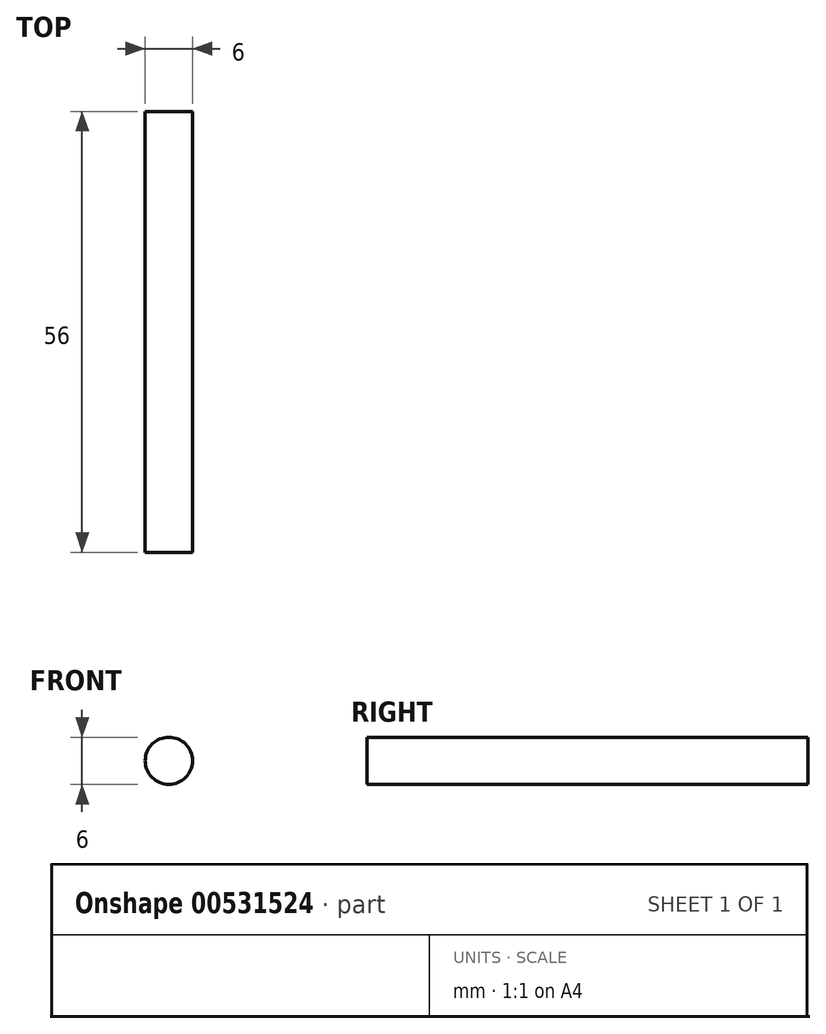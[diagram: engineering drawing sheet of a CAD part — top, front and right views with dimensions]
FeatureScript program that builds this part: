
annotation { "Feature Type Name" : "Feature", "Feature Type Description" : "" }
export const myFeature = defineFeature(function(context is Context, id is Id, definition is map)
    precondition{}
    {
        {
            var Q0;
            Q0=qCreatedBy(makeId("Front.planeOp"),FACE);
            var sketch = newSketch(context, id + "F0", { "sketchPlane" : qUnion([Q0])});
            skCircle(sketch, "E0", {"center": v(-8.48, -29.92) * mm, "radius": 3 * mm});
            skSolve(sketch);
        }
        {
            var Q0;
            Q0 = qSketchRegion(id + "F0", true);
            extrude(context, id + "F1", {"entities" : qUnion([Q0]), "depth" : 56 * mm, "offsetDistance" : 25 * mm});
        }
    });
